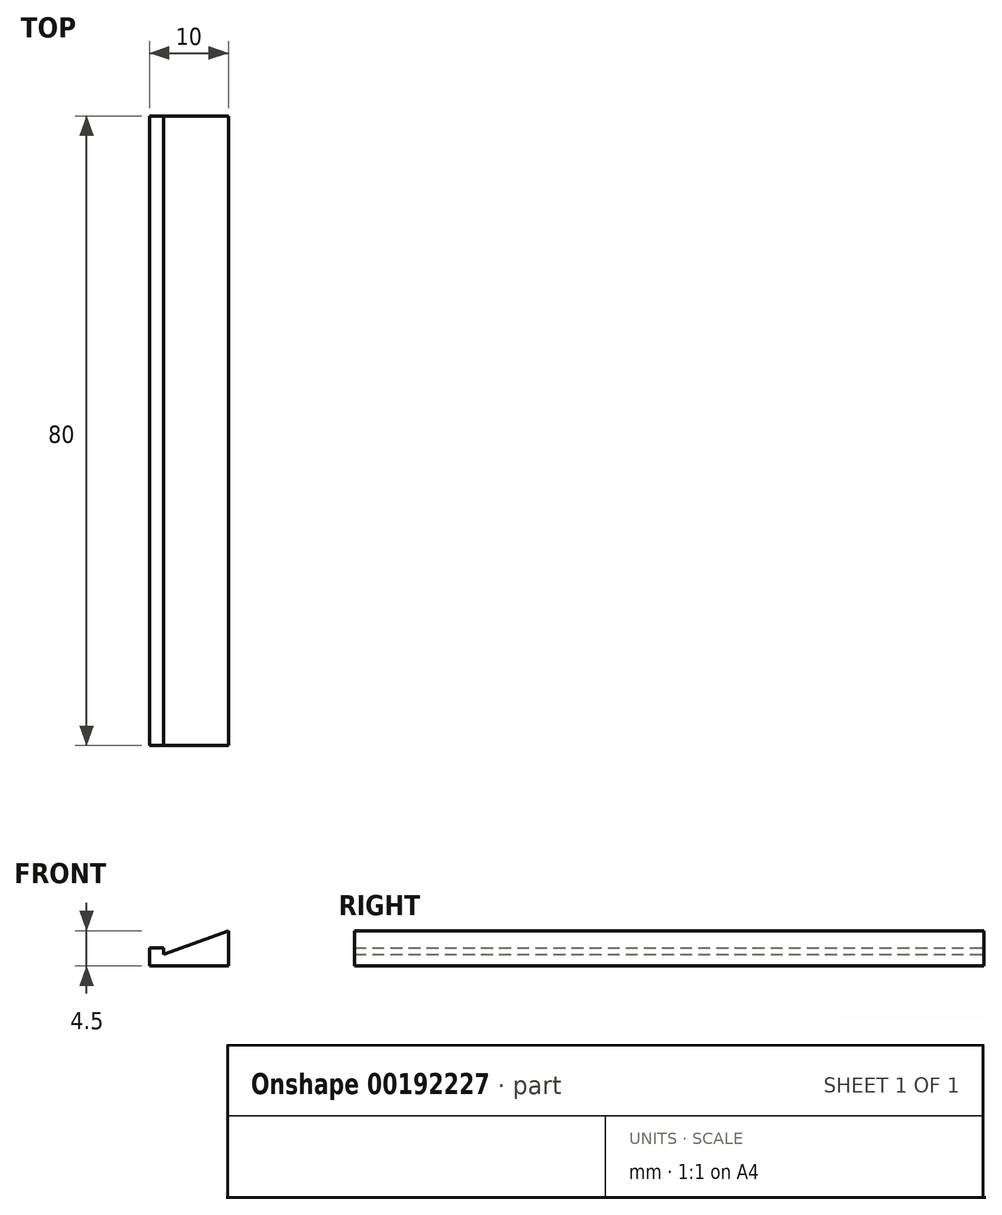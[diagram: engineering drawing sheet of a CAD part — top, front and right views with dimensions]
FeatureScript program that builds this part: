
annotation { "Feature Type Name" : "Feature", "Feature Type Description" : "" }
export const myFeature = defineFeature(function(context is Context, id is Id, definition is map)
    precondition{}
    {
        {
            var Q0;
            Q0=qCreatedBy(makeId("Front.planeOp"),FACE);
            var sketch = newSketch(context, id + "F0", { "sketchPlane" : qUnion([Q0])});
            skLineSegment(sketch, "E0", {"start": v(0, 0) * mm, "end": v(-10, 0) * mm});
            skLineSegment(sketch, "E1", {"start": v(-10, 0) * mm, "end": v(-10, 2.3) * mm});
            skLineSegment(sketch, "E2", {"start": v(-10, 2.3) * mm, "end": v(-8.24, 2.3) * mm});
            skLineSegment(sketch, "E3", {"start": v(-8.24, 2.3) * mm, "end": v(-8.24, 1.5) * mm});
            skLineSegment(sketch, "E4", {"start": v(-8.24, 1.5) * mm, "end": v(0, 4.5) * mm});
            skLineSegment(sketch, "E5", {"start": v(0, 4.5) * mm, "end": v(0, 0) * mm});
            skSolve(sketch);
        }
        {
            var Q0;
            Q0=makeQuery(id+"F0.imprint","IMPRINT",FACE,{"disambiguationData":[TD([[makeQuery(id+"F0.imprint","IMPRINT",EDGE,{"derivedFrom":sQuery(id+"F0.wireOp",EDGE,"E0")}),-1.0]])]});
            extrude(context, id + "F1", {"entities" : qUnion([Q0]), "depth" : 80 * mm});
        }
    });
